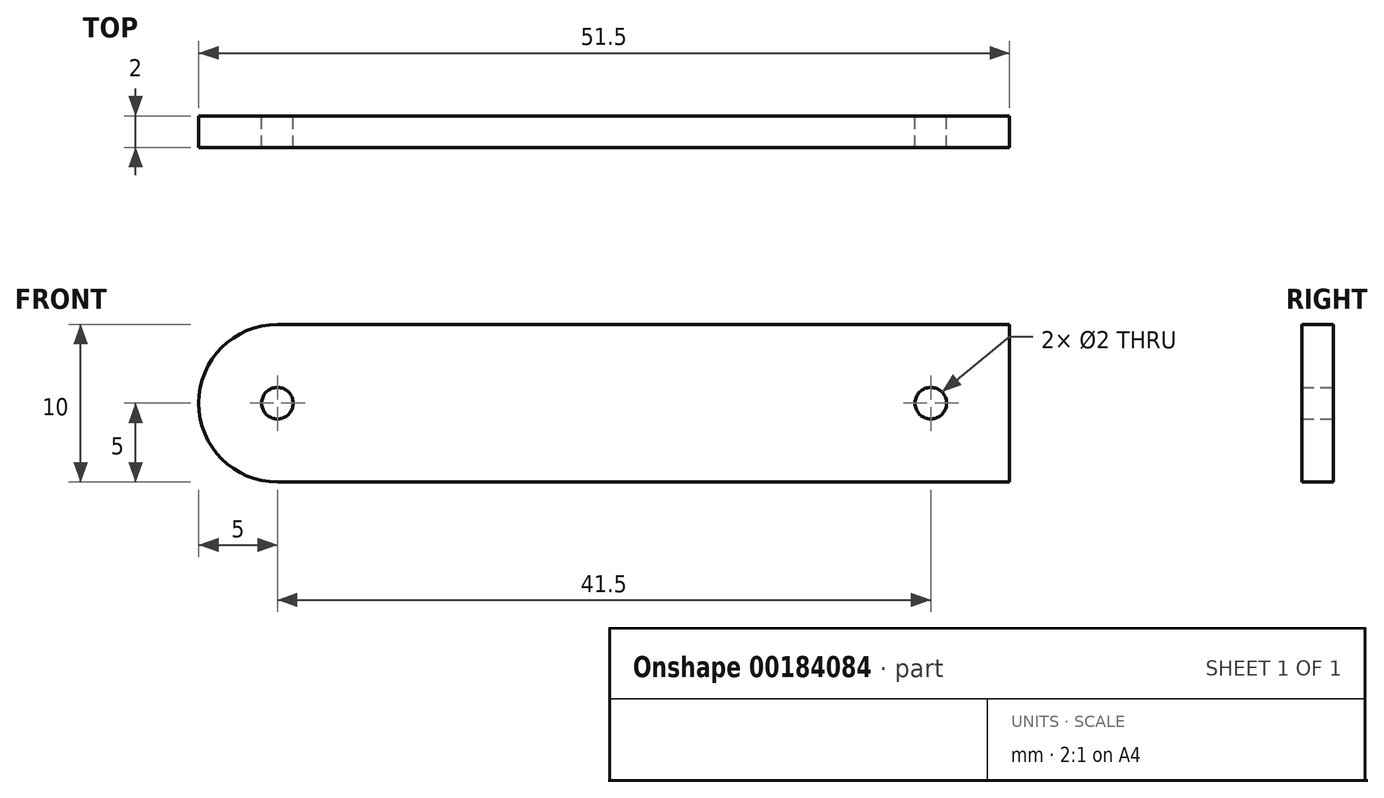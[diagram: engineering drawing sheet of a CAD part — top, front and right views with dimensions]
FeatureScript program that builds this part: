
annotation { "Feature Type Name" : "Feature", "Feature Type Description" : "" }
export const myFeature = defineFeature(function(context is Context, id is Id, definition is map)
    precondition{}
    {
        {
            var Q0;
            Q0=qCreatedBy(makeId("Front.planeOp"),FACE);
            var sketch = newSketch(context, id + "F0", { "sketchPlane" : qUnion([Q0])});
            skLineSegment(sketch, "E0.bottom", {"start": v(0, 0) * mm, "end": v(46.5, 0) * mm});
            skLineSegment(sketch, "E0.top", {"start": v(0, -10) * mm, "end": v(46.5, -10) * mm});
            skLineSegment(sketch, "E0.right", {"start": v(46.5, 0) * mm, "end": v(46.5, -10) * mm});
            skArc(sketch, "E1", {"start": v(0, 0) * mm, "mid": v(-5, -5) * mm, "end": v(0, -10) * mm});
            skCircle(sketch, "E2", {"center": v(0, -5) * mm, "radius": 1 * mm});
            skCircle(sketch, "E3", {"center": v(41.5, -5) * mm, "radius": 1 * mm});
            skSolve(sketch);
        }
        {
            var Q0;
            Q0=makeQuery(id+"F0.imprint","IMPRINT",FACE,{"disambiguationData":[TD([[makeQuery(id+"F0.imprint","IMPRINT",EDGE,{"derivedFrom":sQuery(id+"F0.wireOp",EDGE,"E0.bottom")}),-1.0]])]});
            extrude(context, id + "F1", {"entities" : qUnion([Q0]), "depth" : 2 * mm});
        }
    });
